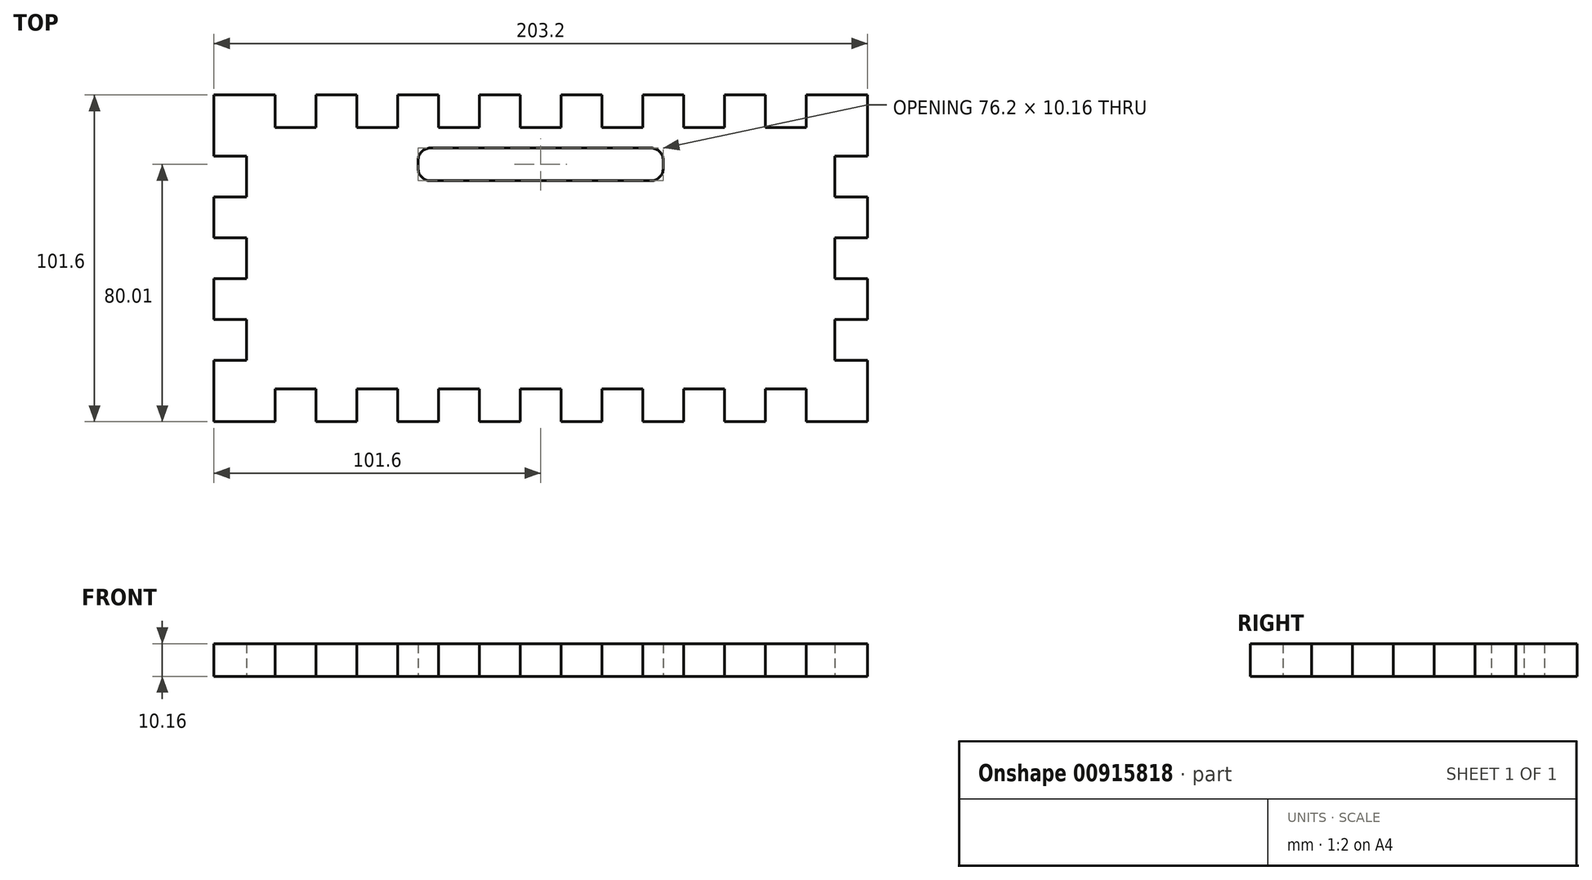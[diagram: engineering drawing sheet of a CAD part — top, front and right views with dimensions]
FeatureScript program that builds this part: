
annotation { "Feature Type Name" : "Feature", "Feature Type Description" : "" }
export const myFeature = defineFeature(function(context is Context, id is Id, definition is map)
    precondition{}
    {
        {
            var Q0;
            Q0=qCreatedBy(makeId("Top.planeOp"),FACE);
            var sketch = newSketch(context, id + "F0", { "sketchPlane" : qUnion([Q0])});
            skLineSegment(sketch, "E0.bottom", {"start": v(0, 0) * mm, "end": v(19.05, 0) * mm});
            skLineSegment(sketch, "E0.left", {"start": v(0, 0) * mm, "end": v(0, -19.05) * mm});
            skLineSegment(sketch, "E1", {"start": v(19.05, 0) * mm, "end": v(19.05, -10.16) * mm});
            skLineSegment(sketch, "E2", {"start": v(19.05, -10.16) * mm, "end": v(31.75, -10.16) * mm});
            skLineSegment(sketch, "E3", {"start": v(31.75, -10.16) * mm, "end": v(31.75, 0) * mm});
            skLineSegment(sketch, "E4", {"start": v(31.75, 0) * mm, "end": v(44.45, 0) * mm});
            skLineSegment(sketch, "E5", {"start": v(44.45, 0) * mm, "end": v(44.45, -10.16) * mm});
            skLineSegment(sketch, "E6", {"start": v(44.45, -10.16) * mm, "end": v(57.15, -10.16) * mm});
            skLineSegment(sketch, "E7", {"start": v(57.15, -10.16) * mm, "end": v(57.15, 0) * mm});
            skLineSegment(sketch, "E8", {"start": v(57.15, 0) * mm, "end": v(69.85, 0) * mm});
            skLineSegment(sketch, "E9", {"start": v(69.85, 0) * mm, "end": v(69.85, -10.16) * mm});
            skLineSegment(sketch, "E10", {"start": v(69.85, -10.16) * mm, "end": v(82.55, -10.16) * mm});
            skLineSegment(sketch, "E11", {"start": v(82.55, -10.16) * mm, "end": v(82.55, 0) * mm});
            skLineSegment(sketch, "E12.trimOffspring", {"start": v(82.55, 0) * mm, "end": v(95.25, 0) * mm});
            skLineSegment(sketch, "E13", {"start": v(95.25, 0) * mm, "end": v(95.25, -10.16) * mm});
            skLineSegment(sketch, "E14", {"start": v(95.25, -10.16) * mm, "end": v(107.95, -10.16) * mm});
            skLineSegment(sketch, "E15", {"start": v(107.95, -10.16) * mm, "end": v(107.95, 0) * mm});
            skLineSegment(sketch, "E16", {"start": v(107.95, 0) * mm, "end": v(120.65, 0) * mm});
            skLineSegment(sketch, "E17", {"start": v(120.65, 0) * mm, "end": v(120.65, -10.16) * mm});
            skLineSegment(sketch, "E18", {"start": v(120.65, -10.16) * mm, "end": v(133.35, -10.16) * mm});
            skLineSegment(sketch, "E19", {"start": v(133.35, -10.16) * mm, "end": v(133.35, 0) * mm});
            skLineSegment(sketch, "E20", {"start": v(133.35, 0) * mm, "end": v(146.05, 0) * mm});
            skLineSegment(sketch, "E21", {"start": v(146.05, 0) * mm, "end": v(146.05, -10.16) * mm});
            skLineSegment(sketch, "E22", {"start": v(146.05, -10.16) * mm, "end": v(158.75, -10.16) * mm});
            skLineSegment(sketch, "E23", {"start": v(158.75, -10.16) * mm, "end": v(158.75, 0) * mm});
            skLineSegment(sketch, "E24.trimOffspring", {"start": v(158.75, 0) * mm, "end": v(171.45, 0) * mm});
            skLineSegment(sketch, "E25", {"start": v(171.45, 0) * mm, "end": v(171.45, -10.16) * mm});
            skLineSegment(sketch, "E26", {"start": v(171.45, -10.16) * mm, "end": v(184.15, -10.16) * mm});
            skLineSegment(sketch, "E27", {"start": v(184.15, -10.16) * mm, "end": v(184.15, 0) * mm});
            skLineSegment(sketch, "E28.trimOffspring", {"start": v(184.15, 0) * mm, "end": v(203.2, 0) * mm});
            skLineSegment(sketch, "E29", {"start": v(0, -19.05) * mm, "end": v(10.16, -19.05) * mm});
            skLineSegment(sketch, "E30", {"start": v(10.16, -19.05) * mm, "end": v(10.16, -31.75) * mm});
            skLineSegment(sketch, "E31", {"start": v(10.16, -31.75) * mm, "end": v(0, -31.75) * mm});
            skLineSegment(sketch, "E32", {"start": v(0, -31.75) * mm, "end": v(0, -44.45) * mm});
            skLineSegment(sketch, "E33", {"start": v(0, -44.45) * mm, "end": v(10.16, -44.45) * mm});
            skLineSegment(sketch, "E34", {"start": v(10.16, -44.45) * mm, "end": v(10.16, -57.15) * mm});
            skLineSegment(sketch, "E35", {"start": v(10.16, -57.15) * mm, "end": v(0, -57.15) * mm});
            skLineSegment(sketch, "E36", {"start": v(101.6, -10.16) * mm, "end": v(101.6, -10.16) * mm});
            skPoint(sketch, "E37.trimOffspring.end.orphan", {"position": v(0, -101.6) * mm});
            skLineSegment(sketch, "E38", {"start": v(0, -57.15) * mm, "end": v(0, -69.85) * mm});
            skLineSegment(sketch, "E39", {"start": v(0, -69.85) * mm, "end": v(10.16, -69.85) * mm});
            skLineSegment(sketch, "E40", {"start": v(10.16, -69.85) * mm, "end": v(10.16, -82.55) * mm});
            skLineSegment(sketch, "E41", {"start": v(10.16, -82.55) * mm, "end": v(0, -82.55) * mm});
            skLineSegment(sketch, "E42", {"start": v(0, -82.55) * mm, "end": v(0, -101.6) * mm});
            skLineSegment(sketch, "E43", {"start": v(10.16, -50.8) * mm, "end": v(10.16, -50.8) * mm});
            skLineSegment(sketch, "E44.MirrorCS", {"start": v(203.2, 0) * mm, "end": v(203.2, -19.05) * mm});
            skLineSegment(sketch, "E45.MirrorCS", {"start": v(203.2, -19.05) * mm, "end": v(193.04, -19.05) * mm});
            skLineSegment(sketch, "E46.MirrorCS", {"start": v(193.04, -19.05) * mm, "end": v(193.04, -31.75) * mm});
            skLineSegment(sketch, "E47.MirrorCS", {"start": v(193.04, -31.75) * mm, "end": v(203.2, -31.75) * mm});
            skLineSegment(sketch, "E48.MirrorCS", {"start": v(203.2, -31.75) * mm, "end": v(203.2, -44.45) * mm});
            skLineSegment(sketch, "E49.MirrorCS", {"start": v(203.2, -44.45) * mm, "end": v(193.04, -44.45) * mm});
            skLineSegment(sketch, "E50.MirrorCS", {"start": v(193.04, -44.45) * mm, "end": v(193.04, -57.15) * mm});
            skLineSegment(sketch, "E51.MirrorCS", {"start": v(193.04, -57.15) * mm, "end": v(203.2, -57.15) * mm});
            skLineSegment(sketch, "E52.MirrorCS", {"start": v(203.2, -57.15) * mm, "end": v(203.2, -69.85) * mm});
            skLineSegment(sketch, "E53.MirrorCS", {"start": v(203.2, -69.85) * mm, "end": v(193.04, -69.85) * mm});
            skLineSegment(sketch, "E54.MirrorCS", {"start": v(193.04, -69.85) * mm, "end": v(193.04, -82.55) * mm});
            skLineSegment(sketch, "E55.MirrorCS", {"start": v(193.04, -82.55) * mm, "end": v(203.2, -82.55) * mm});
            skLineSegment(sketch, "E56.MirrorCS", {"start": v(203.2, -82.55) * mm, "end": v(203.2, -101.6) * mm});
            skLineSegment(sketch, "E57.MirrorCS", {"start": v(0, -101.6) * mm, "end": v(19.05, -101.6) * mm});
            skLineSegment(sketch, "E58.MirrorCS", {"start": v(19.05, -101.6) * mm, "end": v(19.05, -91.44) * mm});
            skLineSegment(sketch, "E59.MirrorCS", {"start": v(19.05, -91.44) * mm, "end": v(31.75, -91.44) * mm});
            skLineSegment(sketch, "E60.MirrorCS", {"start": v(31.75, -91.44) * mm, "end": v(31.75, -101.6) * mm});
            skLineSegment(sketch, "E61.MirrorCS", {"start": v(31.75, -101.6) * mm, "end": v(44.45, -101.6) * mm});
            skLineSegment(sketch, "E62.MirrorCS", {"start": v(44.45, -101.6) * mm, "end": v(44.45, -91.44) * mm});
            skLineSegment(sketch, "E63.MirrorCS", {"start": v(44.45, -91.44) * mm, "end": v(57.15, -91.44) * mm});
            skLineSegment(sketch, "E64.MirrorCS", {"start": v(57.15, -91.44) * mm, "end": v(57.15, -101.6) * mm});
            skLineSegment(sketch, "E65.MirrorCS", {"start": v(57.15, -101.6) * mm, "end": v(69.85, -101.6) * mm});
            skLineSegment(sketch, "E66.MirrorCS", {"start": v(69.85, -101.6) * mm, "end": v(69.85, -91.44) * mm});
            skLineSegment(sketch, "E67.MirrorCS", {"start": v(69.85, -91.44) * mm, "end": v(82.55, -91.44) * mm});
            skLineSegment(sketch, "E68.MirrorCS", {"start": v(82.55, -91.44) * mm, "end": v(82.55, -101.6) * mm});
            skLineSegment(sketch, "E69.MirrorCS", {"start": v(82.55, -101.6) * mm, "end": v(95.25, -101.6) * mm});
            skLineSegment(sketch, "E70.MirrorCS", {"start": v(95.25, -101.6) * mm, "end": v(95.25, -91.44) * mm});
            skLineSegment(sketch, "E71.MirrorCS", {"start": v(95.25, -91.44) * mm, "end": v(107.95, -91.44) * mm});
            skLineSegment(sketch, "E72.MirrorCS", {"start": v(107.95, -91.44) * mm, "end": v(107.95, -101.6) * mm});
            skLineSegment(sketch, "E73.MirrorCS", {"start": v(107.95, -101.6) * mm, "end": v(120.65, -101.6) * mm});
            skLineSegment(sketch, "E74.MirrorCS", {"start": v(120.65, -101.6) * mm, "end": v(120.65, -91.44) * mm});
            skLineSegment(sketch, "E75.MirrorCS", {"start": v(120.65, -91.44) * mm, "end": v(133.35, -91.44) * mm});
            skLineSegment(sketch, "E76.MirrorCS", {"start": v(133.35, -91.44) * mm, "end": v(133.35, -101.6) * mm});
            skLineSegment(sketch, "E77.MirrorCS", {"start": v(133.35, -101.6) * mm, "end": v(146.05, -101.6) * mm});
            skLineSegment(sketch, "E78.MirrorCS", {"start": v(146.05, -101.6) * mm, "end": v(146.05, -91.44) * mm});
            skLineSegment(sketch, "E79.MirrorCS", {"start": v(146.05, -91.44) * mm, "end": v(158.75, -91.44) * mm});
            skLineSegment(sketch, "E80.MirrorCS", {"start": v(158.75, -91.44) * mm, "end": v(158.75, -101.6) * mm});
            skLineSegment(sketch, "E81.MirrorCS", {"start": v(158.75, -101.6) * mm, "end": v(171.45, -101.6) * mm});
            skLineSegment(sketch, "E82.MirrorCS", {"start": v(171.45, -101.6) * mm, "end": v(171.45, -91.44) * mm});
            skLineSegment(sketch, "E83.MirrorCS", {"start": v(171.45, -91.44) * mm, "end": v(184.15, -91.44) * mm});
            skLineSegment(sketch, "E84.MirrorCS", {"start": v(184.15, -91.44) * mm, "end": v(184.15, -101.6) * mm});
            skLineSegment(sketch, "E85.MirrorCS", {"start": v(184.15, -101.6) * mm, "end": v(203.2, -101.6) * mm});
            skLineSegment(sketch, "E86.bottom", {"start": v(67.31, -16.51) * mm, "end": v(135.9, -16.5) * mm});
            skLineSegment(sketch, "E86.top", {"start": v(67.31, -26.67) * mm, "end": v(135.9, -26.67) * mm});
            skLineSegment(sketch, "E86.left", {"start": v(63.5, -20.32) * mm, "end": v(63.5, -22.86) * mm});
            skLineSegment(sketch, "E86.right", {"start": v(139.7, -20.32) * mm, "end": v(139.7, -22.86) * mm});
            skLineSegment(sketch, "E87", {"start": v(101.6, -10.16) * mm, "end": v(101.6, -16.5) * mm, "construction": true});
            skPoint(sketch, "E88.visualSharp", {"position": v(63.5, -16.51) * mm});
            skArc(sketch, "E88.filletArc", {"start": v(67.31, -16.51) * mm, "mid": v(64.62, -17.63) * mm, "end": v(63.5, -20.32) * mm});
            skPoint(sketch, "E89.visualSharp", {"position": v(63.5, -26.67) * mm});
            skArc(sketch, "E89.filletArc", {"start": v(63.5, -22.86) * mm, "mid": v(64.62, -25.55) * mm, "end": v(67.31, -26.67) * mm});
            skPoint(sketch, "E90.visualSharp", {"position": v(139.7, -16.5) * mm});
            skArc(sketch, "E90.filletArc", {"start": v(139.7, -20.32) * mm, "mid": v(138.58, -17.63) * mm, "end": v(135.9, -16.5) * mm});
            skPoint(sketch, "E91.visualSharp", {"position": v(139.7, -26.67) * mm});
            skArc(sketch, "E91.filletArc", {"start": v(135.9, -26.67) * mm, "mid": v(138.58, -25.55) * mm, "end": v(139.7, -22.86) * mm});
            skSolve(sketch);
        }
        {
            var Q0;
            Q0=makeQuery(id+"F0.imprint","IMPRINT",FACE,{"disambiguationData":[TD([[makeQuery(id+"F0.imprint","IMPRINT",EDGE,{"derivedFrom":sQuery(id+"F0.wireOp",EDGE,"E0.bottom")}),-1.0]])]});
            extrude(context, id + "F1", {"entities" : qUnion([Q0]), "depth" : 10.16 * mm, "offsetDistance" : 25.4 * mm});
        }
    });
